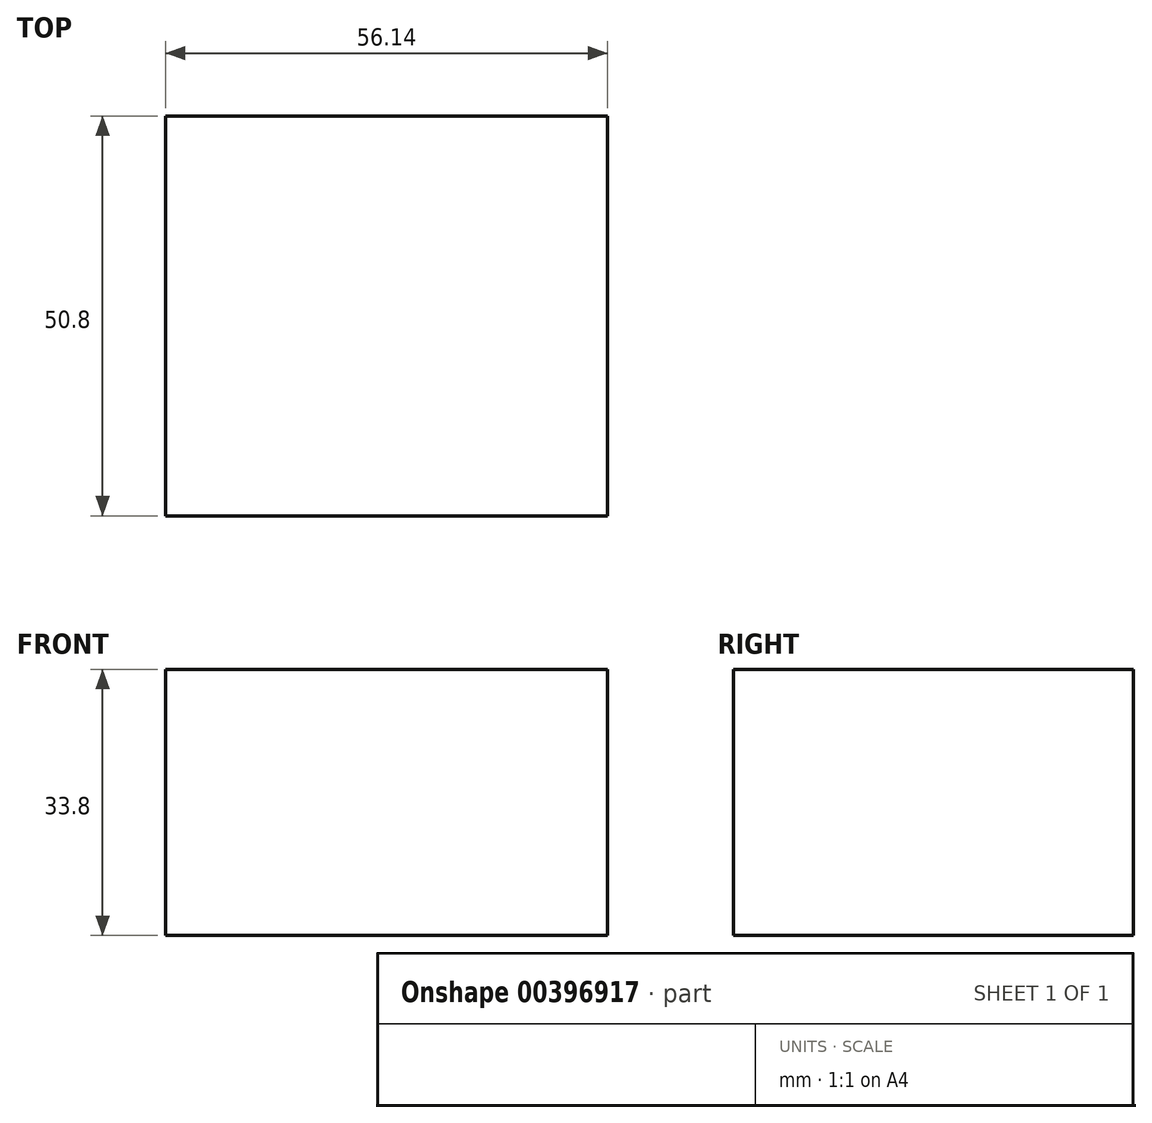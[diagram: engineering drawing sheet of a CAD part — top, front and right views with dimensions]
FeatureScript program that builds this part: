
annotation { "Feature Type Name" : "Feature", "Feature Type Description" : "" }
export const myFeature = defineFeature(function(context is Context, id is Id, definition is map)
    precondition{}
    {
        {
            var Q0;
            Q0=qCreatedBy(makeId("Front.planeOp"),FACE);
            var sketch = newSketch(context, id + "F0", { "sketchPlane" : qUnion([Q0])});
            skLineSegment(sketch, "E0.bottom", {"start": v(0, 0) * mm, "end": v(-56.14, 0) * mm});
            skLineSegment(sketch, "E0.top", {"start": v(0, 33.8) * mm, "end": v(-56.14, 33.8) * mm});
            skLineSegment(sketch, "E0.left", {"start": v(0, 0) * mm, "end": v(0, 33.8) * mm});
            skLineSegment(sketch, "E0.right", {"start": v(-56.14, 0) * mm, "end": v(-56.14, 33.8) * mm});
            skSolve(sketch);
        }
        {
            var Q0;
            Q0=makeQuery(id+"F0.imprint","IMPRINT",FACE,{"disambiguationData":[TD([[makeQuery(id+"F0.imprint","IMPRINT",EDGE,{"derivedFrom":sQuery(id+"F0.wireOp",EDGE,"E0.bottom")}),-1.0]])]});
            extrude(context, id + "F1", {"entities" : qUnion([Q0]), "depth" : 50.8 * mm});
        }
    });
